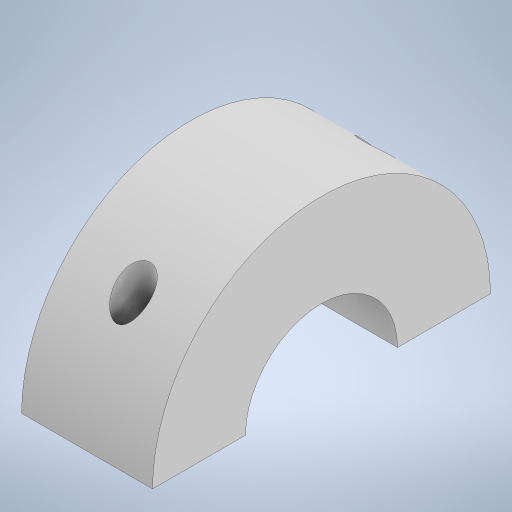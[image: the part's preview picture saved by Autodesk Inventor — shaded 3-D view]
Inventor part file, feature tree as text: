
AUTODESK INVENTOR PART (.ipt)
format: ipt  version: 2023 (Build 270158000, 158)  size: 236,032 bytes
history: native  units: mm
features: extrude x2, sketch x2, projected_geometry x2, plane x1
ambient origin geometry x8: Origin, YZ Plane, XZ Plane, XY Plane, X Axis, Y Axis, Z Axis, Center Point
bodies: Solid1 (feature_tree)
feature tree (7):
  extrude  "Extrusion1"  Depth=40.0mm
  plane  "Work Plane1"
  extrude  "Extrusion2"  Depth=4.0mm
  sketch  "Sketch1"  dims[d0=18.0mm d1=40.0mm]
  sketch  "Sketch2"  dims[d4=15.5mm d5=0.0mm d6=4.0mm d7=4.0mm d8=0.0mm d9=0.0mm d10=11.0mm d11=11.0mm]
  projected_geometry  "Projected Loop1"
  projected_geometry  "Projected Loop2"
